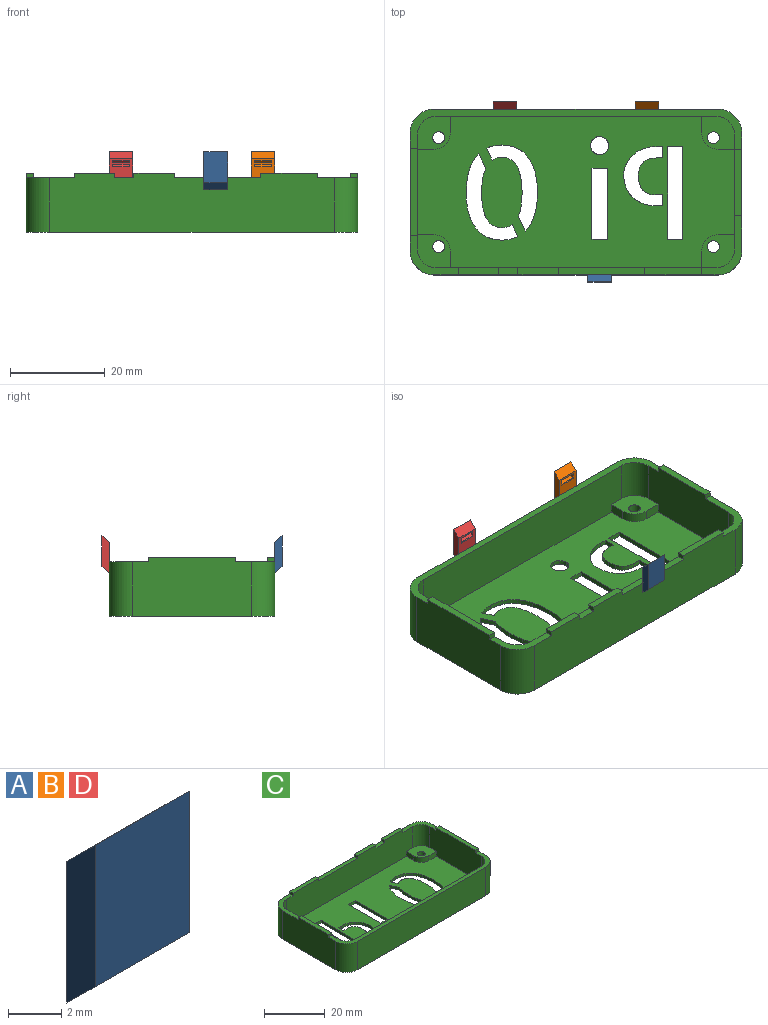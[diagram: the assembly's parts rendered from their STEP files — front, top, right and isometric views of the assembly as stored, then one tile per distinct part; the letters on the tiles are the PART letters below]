
ASSEMBLY  parts=4 mates=3
PART A: 13 faces, bbox 5x1.5x8 mm
  f0: plane 6.5x5mm, normal (0,1,0), area 28.1mm2, adj f1,f2,f4,f5,f6,f7,f8,f9
  f1: plane 8x1.5mm, normal (1,0,0), area 9.8mm2, adj f0,f3,f4,f5
  f2: plane 8x1.5mm, normal (-1,0,0), area 9.8mm2, adj f0,f3,f4,f5
  f3: plane 6.5x5mm, normal (0,-1,0), area 32.5mm2, adj f1,f2,f4,f5
  f4: plane 5x1.5mm, normal (0,0.71,0.71), area 10.6mm2, adj f0,f1,f2,f3
  f5: plane 5x1.5mm, normal (0,-0.71,-0.71), area 10.6mm2, adj f0,f1,f2,f3
  f6: plane 3.5x0.25mm, normal (0,0,1), area 0.9mm2, adj f0,f7,f9,f12
  f7: plane 1.25x0.75mm, normal (1,0,0), area 0.7mm2, adj f0,f6,f8,f10,f11,f12
  f8: plane 3.5x0.25mm, normal (0,0,-1), area 0.9mm2, adj f0,f7,f9,f11
  f9: plane 1.25x0.75mm, normal (-1,0,0), area 0.7mm2, adj f0,f6,f8,f10,f11,f12
  f10: plane 3.5x0.25mm, normal (0,1,0), area 0.9mm2, adj f7,f9,f11,f12
  f11: plane 3.5x0.5mm, normal (0,0.71,-0.71), area 2.5mm2, adj f7,f8,f9,f10
  f12: plane 3.5x0.5mm, normal (0,0.71,0.71), area 2.5mm2, adj f6,f7,f9,f10
PART B: same geometry as A
PART C: 129 faces, bbox 70x35x12.5 mm
  f0: plane 70x35mm, normal (0,0,-1), area 2104.1mm2, adj f7,f8,f9,f10,f31,f32,f33,f34
  f1: plane 67x32mm, normal (0,0,1), area 1653.8mm2, adj f11,f13,f14,f15,f17,f18,f19,f20
  f2: plane 70x8.54mm, normal (0,0,1), area 121.8mm2, adj f8,f9,f10,f18,f19,f22,f29,f30
  f3: plane 10.15x8.25mm, normal (0,0,1), area 23.4mm2, adj f7,f8,f20,f22,f27,f31,f41,f48
  f4: plane 4.1x1.5mm, normal (0,0,1), area 6.2mm2, adj f7,f20,f38,f42
  f5: plane 18.25x1.5mm, normal (0,0,1), area 27.4mm2, adj f7,f20,f35,f39
  f6: plane 12.46x8.5mm, normal (0,0,1), area 27.3mm2, adj f7,f10,f18,f20,f28,f34,f36,f44
  f7: plane 60x12.5mm, normal (0,1,0), area 719mm2, adj f0,f3,f4,f5,f6,f31,f34,f35
  f8: plane 25x12.5mm, normal (1,0,0), area 306mm2, adj f0,f2,f3,f31,f32,f47,f48,f49
  f9: plane 60x11.5mm, normal (0,-1,0), area 690mm2, adj f0,f2,f32,f33
  f10: plane 25x12.5mm, normal (-1,0,0), area 301.5mm2, adj f0,f2,f6,f33,f34,f44,f45,f46
  f11: plane 3.5x2mm, normal (0,1,0), area 7mm2, adj f1,f12,f22,f50
  f12: plane 7x7mm, normal (0,0,1), area 38mm2, adj f11,f13,f19,f22,f30,f50,f57
  f13: plane 3.5x2mm, normal (-1,0,0), area 7mm2, adj f1,f12,f19,f50
  f14: plane 3.5x2mm, normal (0,1,0), area 7mm2, adj f1,f18,f26,f51
  f15: plane 3.5x2mm, normal (0,-1,0), area 7mm2, adj f1,f16,f18,f52
  f16: plane 7x7mm, normal (0,0,1), area 38mm2, adj f15,f17,f18,f20,f28,f52,f56
  f17: plane 3.5x2mm, normal (1,0,0), area 7mm2, adj f1,f16,f20,f52
  f18: plane 24x11.5mm, normal (1,0,0), area 254mm2, adj f1,f2,f6,f14,f15,f16,f26,f28
  f19: plane 59x10.5mm, normal (0,1,0), area 607.5mm2, adj f1,f2,f12,f13,f25,f26,f29,f30
  f20: plane 59x11.5mm, normal (0,-1,0), area 636.5mm2, adj f1,f3,f4,f5,f6,f16,f17,f21
  f21: plane 3.5x2mm, normal (-1,0,0), area 7mm2, adj f1,f20,f24,f53
  f22: plane 24x11.5mm, normal (-1,0,0), area 258.5mm2, adj f1,f2,f3,f11,f12,f23,f24,f27
  f23: plane 3.5x2mm, normal (0,-1,0), area 7mm2, adj f1,f22,f24,f53
  f24: plane 7x7mm, normal (0,0,1), area 38mm2, adj f20,f21,f22,f23,f27,f53,f55
  f25: plane 3.5x2mm, normal (1,0,0), area 7mm2, adj f1,f19,f26,f51
  f26: plane 7x7mm, normal (0,0,1), area 38mm2, adj f14,f18,f19,f25,f29,f51,f54
  f27: cylinder r=4mm len=8.5mm, axis (0,0,-1), area 53.4mm2, adj f3,f20,f22,f24
  f28: cylinder r=4mm len=8.5mm, axis (0,0,1), area 53.4mm2, adj f6,f16,f18,f20
  f29: cylinder r=4mm len=8.5mm, axis (0,0,-1), area 53.4mm2, adj f2,f18,f19,f26
  f30: cylinder r=4mm len=8.5mm, axis (0,0,1), area 53.4mm2, adj f2,f12,f19,f22
  f31: cylinder r=5mm len=11.5mm, axis (0,0,1), area 90.3mm2, adj f0,f3,f7,f8
  f32: cylinder r=5mm len=11.5mm, axis (0,0,-1), area 90.3mm2, adj f0,f2,f8,f9
  f33: cylinder r=5mm len=11.5mm, axis (0,0,1), area 90.3mm2, adj f0,f2,f9,f10
  f34: cylinder r=5mm len=11.5mm, axis (0,0,-1), area 90.3mm2, adj f0,f6,f7,f10
  f35: plane 1.5x1mm, normal (1,0,0), area 1.5mm2, adj f5,f7,f20,f37
  f36: plane 1.5x1mm, normal (-1,0,0), area 1.5mm2, adj f6,f7,f20,f37
  f37: plane 12x1.5mm, normal (0,0,1), area 18mm2, adj f7,f20,f35,f36
  f38: plane 1.5x1mm, normal (1,0,0), area 1.5mm2, adj f4,f7,f20,f40
  f39: plane 1.5x1mm, normal (-1,0,0), area 1.5mm2, adj f5,f7,f20,f40
  f40: plane 8.5x1.5mm, normal (0,0,1), area 12.8mm2, adj f7,f20,f38,f39
  f41: plane 1.5x1mm, normal (1,0,0), area 1.5mm2, adj f3,f7,f20,f43
  f42: plane 1.5x1mm, normal (-1,0,0), area 1.5mm2, adj f4,f7,f20,f43
  f43: plane 8.5x1.5mm, normal (0,0,1), area 12.8mm2, adj f7,f20,f41,f42
  f44: plane 1.5x1mm, normal (0,1,0), area 1.5mm2, adj f6,f10,f18,f46
  f45: plane 1.5x1mm, normal (0,-1,0), area 1.5mm2, adj f2,f10,f18,f46
  f46: plane 14x1.5mm, normal (0,0,1), area 21mm2, adj f10,f18,f44,f45
  f47: plane 1.5x1mm, normal (0,-1,0), area 1.5mm2, adj f2,f8,f22,f49
  f48: plane 1.5x1mm, normal (0,1,0), area 1.5mm2, adj f3,f8,f22,f49
  f49: plane 18.5x1.5mm, normal (0,0,1), area 27.8mm2, adj f8,f22,f47,f48
  f50: cylinder r=3.5mm len=3.5mm, axis (0,0,1), area 11mm2, adj f1,f11,f12,f13
  f51: cylinder r=3.5mm len=3.5mm, axis (0,0,1), area 11mm2, adj f1,f14,f25,f26
  f52: cylinder r=3.5mm len=3.5mm, axis (0,0,1), area 11mm2, adj f1,f15,f16,f17
  f53: cylinder r=3.5mm len=3.5mm, axis (0,0,1), area 11mm2, adj f1,f21,f23,f24
  f54: cylinder r=1.25mm len=3mm, axis (0,0,1), area 23.6mm2, adj f0,f26
  f55: cylinder r=1.25mm len=3mm, axis (0,0,1), area 23.6mm2, adj f0,f24
  f56: cylinder r=1.25mm len=3mm, axis (0,0,1), area 23.6mm2, adj f0,f16
  f57: cylinder r=1.25mm len=3mm, axis (0,0,1), area 23.6mm2, adj f0,f12
  f58: extruded ~1.78x1mm, area 1.8mm2, adj f0,f1,f59,f73
  f59: extruded ~1.97x1mm, area 2.1mm2, adj f0,f1,f58,f60
  f60: plane 2.51x1.17mm, normal (-0.91,-0.42,0), area 2.8mm2, adj f0,f1,f59,f61
  f61: extruded ~3.22x1mm, area 3.3mm2, adj f0,f1,f60,f62
  f62: extruded ~3.13x1mm, area 3.2mm2, adj f0,f1,f61,f63
  f63: extruded ~2.37x1.9mm, area 3.1mm2, adj f0,f1,f62,f64
  f64: extruded ~3.13x1.49mm, area 3.5mm2, adj f0,f1,f63,f65
  f65: extruded ~4.35x1mm, area 4.4mm2, adj f0,f1,f64,f66
  f66: extruded ~4.86x1mm, area 4.9mm2, adj f0,f1,f65,f67
  f67: extruded ~3.26x1.89mm, area 3.8mm2, adj f0,f1,f66,f68
  f68: plane 3.11x1.46mm, normal (-0.91,-0.42,0), area 3.4mm2, adj f0,f1,f67,f69
  f69: extruded ~2.13x1mm, area 2.2mm2, adj f0,f1,f68,f70
  f70: extruded ~2.88x1mm, area 2.9mm2, adj f0,f1,f69,f71
  f71: extruded ~3.46x1mm, area 3.5mm2, adj f0,f1,f70,f72
  f72: extruded ~2.31x1mm, area 2.5mm2, adj f0,f1,f71,f73
  f73: extruded ~1.36x1.27mm, area 1.9mm2, adj f0,f1,f58,f72
  f74: extruded ~1.34x1mm, area 1.5mm2, adj f0,f1,f75,f81
  f75: extruded ~1.36x1mm, area 1.5mm2, adj f0,f1,f74,f76
  f76: extruded ~1.36x1mm, area 1.5mm2, adj f0,f1,f75,f77
  f77: extruded ~1.33x1mm, area 1.5mm2, adj f0,f1,f76,f78
  f78: extruded ~1.36x1mm, area 1.5mm2, adj f0,f1,f77,f79
  f79: extruded ~1.33x1mm, area 1.5mm2, adj f0,f1,f78,f80
  f80: extruded ~1.35x1mm, area 1.5mm2, adj f0,f1,f79,f81
  f81: extruded ~1.36x1mm, area 1.5mm2, adj f0,f1,f74,f80
  f82: plane 3.25x1mm, normal (0,-1,0), area 3.3mm2, adj f0,f1,f83,f85
  f83: plane 15.02x1mm, normal (-1,0,0), area 15mm2, adj f0,f1,f82,f84
  f84: plane 3.25x1mm, normal (0,1,0), area 3.3mm2, adj f0,f1,f83,f85
  f85: plane 15.02x1mm, normal (1,0,0), area 15mm2, adj f0,f1,f82,f84
  f86: extruded ~2.48x1mm, area 2.5mm2, adj f0,f1,f87,f107
  f87: plane 1.36x1mm, normal (0,1,0), area 1.4mm2, adj f0,f1,f86,f88
  f88: plane 2.42x1mm, normal (1,0,0), area 2.4mm2, adj f0,f1,f87,f89
  f89: plane 1.3x1mm, normal (0,-1,0), area 1.3mm2, adj f0,f1,f88,f90
  f90: extruded ~1.97x1mm, area 2mm2, adj f0,f1,f89,f91
  f91: extruded ~1.16x1mm, area 1.5mm2, adj f0,f1,f90,f92
  f92: extruded ~1.2x1mm, area 1.3mm2, adj f0,f1,f91,f93
  f93: extruded ~1.11x1mm, area 1.1mm2, adj f0,f1,f92,f94
  f94: extruded ~2.01x1mm, area 2mm2, adj f0,f1,f93,f95
  f95: extruded ~1.27x1mm, area 1.5mm2, adj f0,f1,f94,f96
  f96: extruded ~1.05x1mm, area 1.2mm2, adj f0,f1,f95,f97
  f97: extruded ~1.16x1mm, area 1.2mm2, adj f0,f1,f96,f98
  f98: plane 1.84x1mm, normal (0,1,0), area 1.8mm2, adj f0,f1,f97,f99
  f99: plane 2.34x1mm, normal (1,0,0), area 2.3mm2, adj f0,f1,f98,f100
  f100: plane 1.28x1mm, normal (0,-1,0), area 1.3mm2, adj f0,f1,f99,f101
  f101: extruded ~2.83x1mm, area 2.9mm2, adj f0,f1,f100,f102
  f102: extruded ~2.18x1.28mm, area 2.5mm2, adj f0,f1,f101,f103
  f103: extruded ~2.04x1.41mm, area 2.5mm2, adj f0,f1,f102,f104
  f104: extruded ~2.7x1mm, area 2.8mm2, adj f0,f1,f103,f105
  f105: extruded ~2.55x1mm, area 2.6mm2, adj f0,f1,f104,f106
  f106: extruded ~1.93x1.57mm, area 2.5mm2, adj f0,f1,f105,f107
  f107: extruded ~2.2x1.2mm, area 2.5mm2, adj f0,f1,f86,f106
  f108: extruded ~3.27x1.98mm, area 3.9mm2, adj f0,f1,f109,f124
  f109: plane 3.09x1.47mm, normal (0.9,0.43,0), area 3.4mm2, adj f0,f1,f108,f110
  f110: extruded ~1x0.05mm, area 0.1mm2, adj f0,f1,f109,f111
  f111: extruded ~2.13x1mm, area 2.2mm2, adj f0,f1,f110,f112
  f112: extruded ~2.93x1mm, area 2.9mm2, adj f0,f1,f111,f113
  f113: extruded ~3.47x1mm, area 3.5mm2, adj f0,f1,f112,f114
  f114: extruded ~2.3x1mm, area 2.5mm2, adj f0,f1,f113,f115
  f115: extruded ~1.37x1.27mm, area 1.9mm2, adj f0,f1,f114,f116
  f116: extruded ~1.8x1mm, area 1.9mm2, adj f0,f1,f115,f117
  f117: extruded ~2.08x1mm, area 2.2mm2, adj f0,f1,f116,f118
  f118: plane 2.53x1.2mm, normal (0.9,0.43,0), area 2.8mm2, adj f0,f1,f117,f119
  f119: extruded ~3.35x1mm, area 3.5mm2, adj f0,f1,f118,f120
  f120: extruded ~3.14x1mm, area 3.2mm2, adj f0,f1,f119,f121
  f121: extruded ~2.37x1.89mm, area 3.1mm2, adj f0,f1,f120,f122
  f122: extruded ~3.14x1.5mm, area 3.5mm2, adj f0,f1,f121,f123
  f123: extruded ~4.37x1mm, area 4.4mm2, adj f0,f1,f122,f124
  f124: extruded ~4.93x1mm, area 5mm2, adj f0,f1,f108,f123
  f125: plane 3.2x1mm, normal (0,1,0), area 3.2mm2, adj f0,f1,f126,f128
  f126: plane 19.63x1mm, normal (1,0,0), area 19.6mm2, adj f0,f1,f125,f127
  f127: plane 3.2x1mm, normal (0,-1,0), area 3.2mm2, adj f0,f1,f126,f128
  f128: plane 19.63x1mm, normal (-1,0,0), area 19.6mm2, adj f0,f1,f125,f127
PART D: same geometry as A
PLACE A t=(30.31,26.81,22.49)mm
PLACE B rot(axis=(0,0,1),180deg) t=(40.31,61.81,22.49)mm
PLACE C rot(axis=(0,0,-1),180deg) t=(25.31,44.31,9.49)mm
PLACE D rot(axis=(0,0,1),180deg) t=(10.31,61.81,22.49)mm
MATE fastened C.f7 <-> A.f0  axis (0,-1,0) through (30.31,26.81,18.49)mm
MATE fastened D.f0 <-> C.f9  axis (0,-1,0) through (10.31,61.81,18.49)mm
MATE fastened B.f0 <-> C.f9  axis (0,-1,0) through (40.31,61.81,18.49)mm
